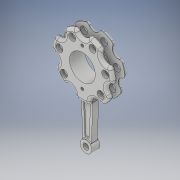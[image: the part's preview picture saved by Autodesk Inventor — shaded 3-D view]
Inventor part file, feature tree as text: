
AUTODESK INVENTOR PART (.ipt)
format: ipt  version: 2018 (Build 220112000, 112)  size: 567,808 bytes
history: native  units: mm
features: sketch x8, extrude x5, fillet x3, plane x1, hole x1, mirror x1
ambient origin geometry x8: Origin, YZ Plane, XZ Plane, XY Plane, X Axis, Y Axis, Z Axis, Center Point
bodies: Solid1 (feature_tree)
feature tree (19):
  extrude  "Extrusion1"  Depth=52.0mm
  sketch  "Sketch2"  dims[d2=41.96mm d3=10.0mm]
  plane  "Work Plane1"
  extrude  "Extrusion2"  Depth=10.0mm
  sketch  "Sketch4"  dims[d9=26.0mm d10=6.0mm]
  sketch  "Sketch5"  dims[d11=20.0mm d15=13.0mm d16=0.0mm d17=28.0mm]
  extrude  "Extrusion3"  Depth=70.0mm TaperAngle=360.0deg
  extrude  "Extrusion4"  Depth=6.0mm
  sketch  "Sketch6"  dims[d18=4.537856mm d19=34.0mm d20=4.537856mm d23=2.0mm]
  hole  "Hole1"  [1 undecoded]
  fillet  "Fillet1"  Radius=28.0mm
  extrude  "Extrusion6"  Depth=34.0mm
  mirror  "Mirror2"
  fillet  "Fillet2"  Radius=4.537856mm
  fillet  "Fillet3"  Radius=2.0mm
  sketch  "Sketch1"  dims[d0=22.0mm d1=52.0mm]
  sketch  "Sketch3"  dims[d4=5.74mm d5=70.0mm d7=360.0deg]
  sketch  "Sketch7"  dims[d26=7.0mm d27=0.0mm]
  sketch  "Sketch8"  dims[d28=60.0mm d29=5.0mm d30=10.0mm d31=9.96mm d32=7.23mm d33=1.93mm d34=1.5mm d36=1.93mm d37=0.94mm d38=0.94mm d39=0.94mm d40=7.0mm d41=0.0mm d42=5.0mm d43=0.0mm d46=16.0mm d47=16.0mm d48=2.459mm d49=6.0mm d50=4.0mm d51=2.0mm d52=90.0deg d53=16.55mm d54=20.594885mm d55=2.5mm d56=0.88mm d57=0.0mm d58=0.5mm d59=0.85mm]
note: 1 required parameter value undecoded (feature->parameter linkage not recoverable at this tier; creation-order binding heuristic only, values carry confidence <= 0.55)
